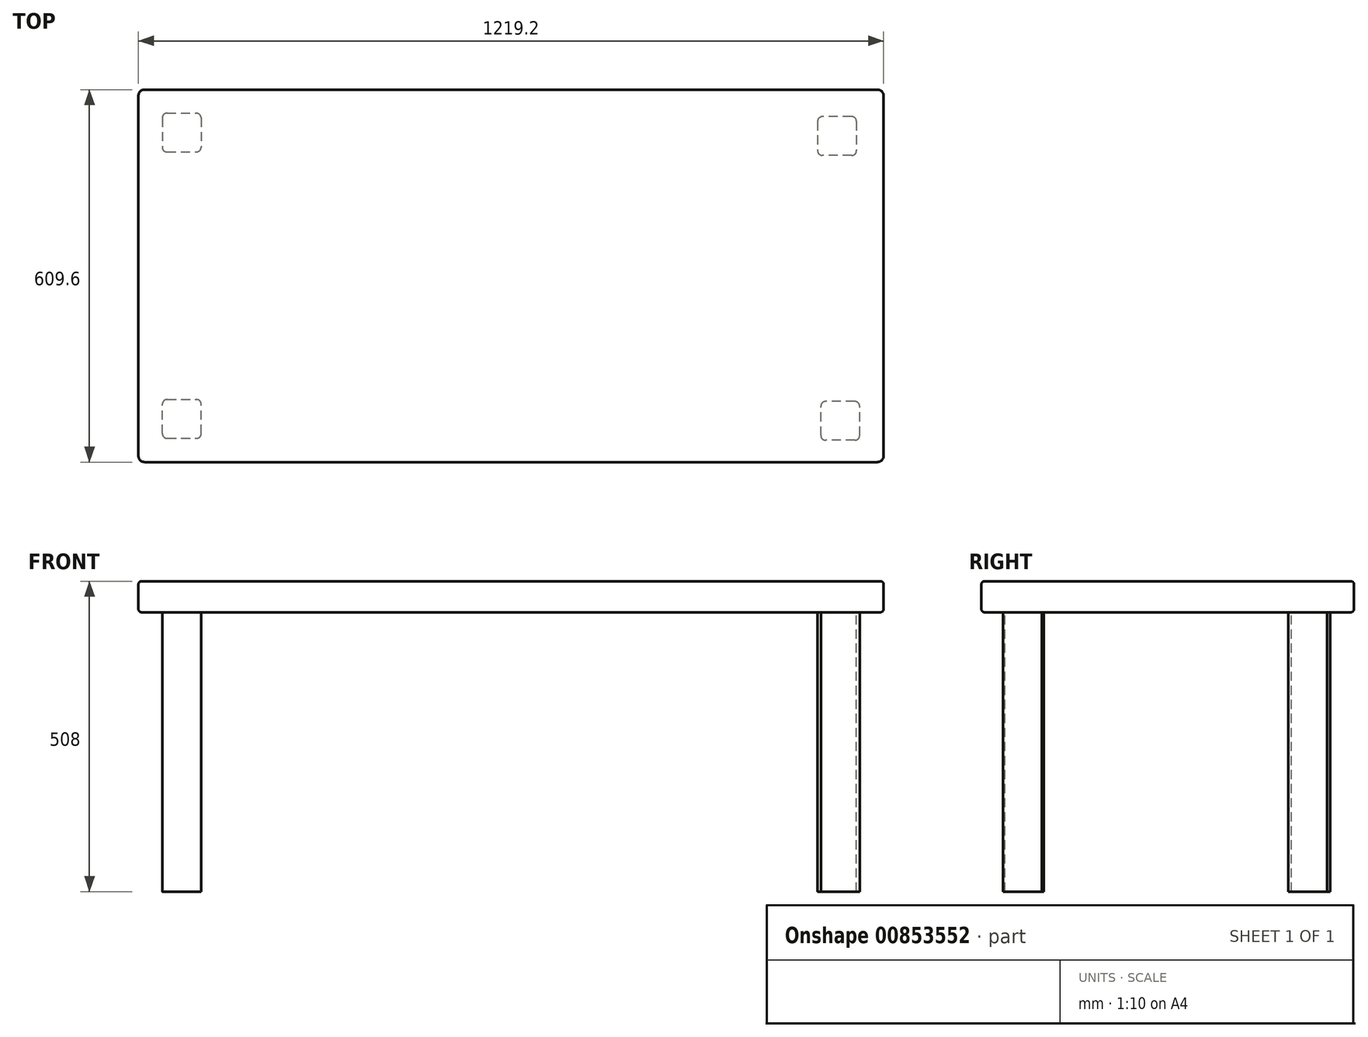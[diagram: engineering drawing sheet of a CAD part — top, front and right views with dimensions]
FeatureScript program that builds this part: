
annotation { "Feature Type Name" : "Feature", "Feature Type Description" : "" }
export const myFeature = defineFeature(function(context is Context, id is Id, definition is map)
    precondition{}
    {
        {
            var Q0;
            Q0=qCreatedBy(makeId("Front.planeOp"),FACE);
            var sketch = newSketch(context, id + "F0", { "sketchPlane" : qUnion([Q0])});
            skLineSegment(sketch, "E0.bottom", {"start": v(609.6, -25.4) * mm, "end": v(-609.6, -25.4) * mm});
            skLineSegment(sketch, "E0.top", {"start": v(609.6, 25.4) * mm, "end": v(-609.6, 25.4) * mm});
            skLineSegment(sketch, "E0.left", {"start": v(609.6, -25.4) * mm, "end": v(609.6, 25.4) * mm});
            skLineSegment(sketch, "E0.right", {"start": v(-609.6, -25.4) * mm, "end": v(-609.6, 25.4) * mm});
            skPoint(sketch, "E0.middle", {"position": v(0, 0) * mm});
            skSolve(sketch);
        }
        {
            var Q0;
            Q0 = qSketchRegion(id + "F0", true);
            extrude(context, id + "F1", {"entities" : qUnion([Q0]), "depth" : 609.6 * mm, "offsetDistance" : 25.4 * mm});
        }
        {
            var Q0;
            Q0=makeQuery(id+"F1.opExtrude","SWEPT_FACE",FACE,{"disambiguationData":[OSD([sQuery(id+"F0.wireOp",EDGE,"E0.bottom")])]});
            var sketch = newSketch(context, id + "F2", { "sketchPlane" : qUnion([Q0])});
            skLineSegment(sketch, "E1.bottom", {"start": v(-571.5, 571.5) * mm, "end": v(571.5, 571.5) * mm, "construction": true});
            skLineSegment(sketch, "E1.top", {"start": v(-571.5, 38.1) * mm, "end": v(571.5, 38.1) * mm, "construction": true});
            skLineSegment(sketch, "E1.left", {"start": v(-571.5, 571.5) * mm, "end": v(-571.5, 38.1) * mm, "construction": true});
            skLineSegment(sketch, "E1.right", {"start": v(571.5, 571.5) * mm, "end": v(571.5, 38.1) * mm, "construction": true});
            skLineSegment(sketch, "E2", {"start": v(-571.5, 571.5) * mm, "end": v(-609.6, 609.6) * mm, "construction": true});
            skLineSegment(sketch, "E3", {"start": v(571.5, 571.5) * mm, "end": v(609.6, 609.6) * mm, "construction": true});
            skLineSegment(sketch, "E4", {"start": v(-609.6, 0) * mm, "end": v(-571.5, 38.1) * mm, "construction": true});
            skLineSegment(sketch, "E5", {"start": v(571.5, 38.1) * mm, "end": v(609.6, 0) * mm, "construction": true});
            skLineSegment(sketch, "E6", {"start": v(0, 571.5) * mm, "end": v(0, 609.6) * mm, "construction": true});
            skLineSegment(sketch, "E7", {"start": v(571.5, 304.8) * mm, "end": v(609.6, 304.8) * mm, "construction": true});
            skLineSegment(sketch, "E8", {"start": v(0, 38.1) * mm, "end": v(0, 0) * mm, "construction": true});
            skLineSegment(sketch, "E9", {"start": v(-571.5, 304.8) * mm, "end": v(-609.6, 304.8) * mm, "construction": true});
            skSolve(sketch);
        }
        {
            var Q0;
            Q0=makeQuery(id+"F1.opExtrude","CAP_EDGE",EDGE,{"disambiguationData":[OSD([sQuery(id+"F0.wireOp",EDGE,"E0.right")])],"isStart":false});
            fillet(context, id + "F3", {"entities" : qUnion([Q0]), "radius" : 10.16 * mm, "tangentPropagation" : true, "allowEdgeOverflow" : false});
        }
        {
            var Q0;
            Q0=makeQuery(id+"F1.opExtrude","CAP_EDGE",EDGE,{"disambiguationData":[OSD([sQuery(id+"F0.wireOp",EDGE,"E0.right")])],"isStart":true});
            fillet(context, id + "F4", {"entities" : qUnion([Q0]), "radius" : 10.16 * mm, "tangentPropagation" : true, "allowEdgeOverflow" : false});
        }
        {
            var Q0;
            Q0=makeQuery(id+"F1.opExtrude","CAP_EDGE",EDGE,{"disambiguationData":[OSD([sQuery(id+"F0.wireOp",EDGE,"E0.left")])],"isStart":true});
            fillet(context, id + "F5", {"entities" : qUnion([Q0]), "radius" : 10.16 * mm, "tangentPropagation" : true, "allowEdgeOverflow" : false});
        }
        {
            var Q0;
            Q0=makeQuery(id+"F1.opExtrude","CAP_EDGE",EDGE,{"disambiguationData":[OSD([sQuery(id+"F0.wireOp",EDGE,"E0.left")])],"isStart":false});
            fillet(context, id + "F6", {"entities" : qUnion([Q0]), "radius" : 10.16 * mm, "tangentPropagation" : true, "allowEdgeOverflow" : false});
        }
        {
            var Q0;
            Q0=makeQuery(id+"F1.opExtrude","SWEPT_EDGE",EDGE,{"disambiguationData":[OSD([sQuery(id+"F0.wireOp",EDGE,"E0.top"),sQuery(id+"F0.wireOp",EDGE,"E0.right")])]});
            var Q1;
            Q1=makeQuery(id+"F1.opExtrude","SWEPT_EDGE",EDGE,{"disambiguationData":[OSD([sQuery(id+"F0.wireOp",EDGE,"E0.bottom"),sQuery(id+"F0.wireOp",EDGE,"E0.right")])]});
            fillet(context, id + "F7", {"entities" : qUnion([Q0, Q1]), "radius" : 5.08 * mm, "tangentPropagation" : true, "allowEdgeOverflow" : false});
        }
        {
            var Q0;
            {var subQ0=sQuery(id+"F0.wireOp",EDGE,"E0.bottom");Q0=makeQuery(id+"F2.imprint","IMPRINT",FACE,{"disambiguationData":[TD([[makeQuery(id+"F2.imprint","IMPRINT",EDGE,{"derivedFrom":makeQuery(id+"F1.opExtrude","CAP_EDGE",EDGE,{"disambiguationData":[OSD([subQ0])],"isStart":true})}),-1.0]])]});}
            var sketch = newSketch(context, id + "F8", { "sketchPlane" : qUnion([Q0])});
            skLineSegment(sketch, "E10.bottom", {"start": v(-570.63, 38.64) * mm, "end": v(-507.13, 38.64) * mm});
            skLineSegment(sketch, "E10.top", {"start": v(-570.63, 102.14) * mm, "end": v(-507.13, 102.14) * mm});
            skLineSegment(sketch, "E10.left", {"start": v(-570.63, 38.64) * mm, "end": v(-570.63, 102.14) * mm});
            skLineSegment(sketch, "E10.right", {"start": v(-507.13, 38.64) * mm, "end": v(-507.13, 102.14) * mm});
            skSolve(sketch);
        }
        {
            var Q0;
            Q0 = qSketchRegion(id + "F8", true);
            extrude(context, id + "F9", {"entities" : qUnion([Q0]), "operationType" : NewBodyOperationType.ADD, "depth" : 457.2 * mm, "offsetDistance" : 25.4 * mm});
        }
        {
            var Q0;
            Q0=makeQuery(id+"F9.opExtrude","SWEPT_EDGE",EDGE,{"disambiguationData":[OSD([sQuery(id+"F8.wireOp",EDGE,"E10.bottom"),sQuery(id+"F8.wireOp",EDGE,"E10.right")])]});
            var Q1;
            Q1=makeQuery(id+"F9.opExtrude","SWEPT_EDGE",EDGE,{"disambiguationData":[OSD([sQuery(id+"F8.wireOp",EDGE,"E10.top"),sQuery(id+"F8.wireOp",EDGE,"E10.right")])]});
            var Q2;
            Q2=makeQuery(id+"F9.opExtrude","SWEPT_EDGE",EDGE,{"disambiguationData":[OSD([sQuery(id+"F8.wireOp",EDGE,"E10.top"),sQuery(id+"F8.wireOp",EDGE,"E10.left")])]});
            var Q3;
            Q3=makeQuery(id+"F9.opExtrude","SWEPT_EDGE",EDGE,{"disambiguationData":[OSD([sQuery(id+"F8.wireOp",EDGE,"E10.bottom"),sQuery(id+"F8.wireOp",EDGE,"E10.left")])]});
            fillet(context, id + "F10", {"entities" : qUnion([Q0, Q1, Q2, Q3]), "radius" : 7.62 * mm, "tangentPropagation" : true, "allowEdgeOverflow" : false});
        }
        {
            var Q0;
            {var subQ0=sQuery(id+"F0.wireOp",EDGE,"E0.bottom");Q0=makeQuery(id+"F2.imprint","IMPRINT",FACE,{"disambiguationData":[TD([[makeQuery(id+"F2.imprint","IMPRINT",EDGE,{"derivedFrom":makeQuery(id+"F1.opExtrude","CAP_EDGE",EDGE,{"disambiguationData":[OSD([subQ0])],"isStart":true})}),-1.0]])]});}
            var sketch = newSketch(context, id + "F11", { "sketchPlane" : qUnion([Q0])});
            skLineSegment(sketch, "E11.bottom", {"start": v(565.21, 44.22) * mm, "end": v(501.71, 44.22) * mm});
            skLineSegment(sketch, "E11.top", {"start": v(565.21, 107.72) * mm, "end": v(501.71, 107.72) * mm});
            skLineSegment(sketch, "E11.left", {"start": v(565.21, 44.22) * mm, "end": v(565.21, 107.72) * mm});
            skLineSegment(sketch, "E11.right", {"start": v(501.71, 44.22) * mm, "end": v(501.71, 107.72) * mm});
            skSolve(sketch);
        }
        {
            var Q0;
            Q0 = qSketchRegion(id + "F11", true);
            extrude(context, id + "F12", {"entities" : qUnion([Q0]), "operationType" : NewBodyOperationType.ADD, "depth" : 457.2 * mm, "offsetDistance" : 25.4 * mm});
        }
        {
            var Q0;
            Q0=makeQuery(id+"F12.opExtrude","SWEPT_EDGE",EDGE,{"disambiguationData":[OSD([sQuery(id+"F11.wireOp",EDGE,"E11.top"),sQuery(id+"F11.wireOp",EDGE,"E11.left")])]});
            var Q1;
            Q1=makeQuery(id+"F12.opExtrude","SWEPT_EDGE",EDGE,{"disambiguationData":[OSD([sQuery(id+"F11.wireOp",EDGE,"E11.bottom"),sQuery(id+"F11.wireOp",EDGE,"E11.left")])]});
            var Q2;
            Q2=makeQuery(id+"F12.opExtrude","SWEPT_EDGE",EDGE,{"disambiguationData":[OSD([sQuery(id+"F11.wireOp",EDGE,"E11.top"),sQuery(id+"F11.wireOp",EDGE,"E11.right")])]});
            var Q3;
            Q3=makeQuery(id+"F12.opExtrude","SWEPT_EDGE",EDGE,{"disambiguationData":[OSD([sQuery(id+"F11.wireOp",EDGE,"E11.bottom"),sQuery(id+"F11.wireOp",EDGE,"E11.right")])]});
            fillet(context, id + "F13", {"entities" : qUnion([Q0, Q1, Q2, Q3]), "radius" : 7.62 * mm, "tangentPropagation" : true, "allowEdgeOverflow" : false});
        }
        {
            var Q0;
            {var subQ0=sQuery(id+"F0.wireOp",EDGE,"E0.bottom");Q0=makeQuery(id+"F2.imprint","IMPRINT",FACE,{"disambiguationData":[TD([[makeQuery(id+"F2.imprint","IMPRINT",EDGE,{"derivedFrom":makeQuery(id+"F1.opExtrude","CAP_EDGE",EDGE,{"disambiguationData":[OSD([subQ0])],"isStart":true})}),-1.0]])]});}
            var sketch = newSketch(context, id + "F14", { "sketchPlane" : qUnion([Q0])});
            skLineSegment(sketch, "E12.bottom", {"start": v(-570.37, 570.76) * mm, "end": v(-506.87, 570.76) * mm});
            skLineSegment(sketch, "E12.top", {"start": v(-570.37, 507.26) * mm, "end": v(-506.87, 507.26) * mm});
            skLineSegment(sketch, "E12.left", {"start": v(-570.37, 570.76) * mm, "end": v(-570.37, 507.26) * mm});
            skLineSegment(sketch, "E12.right", {"start": v(-506.87, 570.76) * mm, "end": v(-506.87, 507.26) * mm});
            skSolve(sketch);
        }
        {
            var Q0;
            Q0 = qSketchRegion(id + "F14", true);
            extrude(context, id + "F15", {"entities" : qUnion([Q0]), "operationType" : NewBodyOperationType.ADD, "depth" : 457.2 * mm, "offsetDistance" : 25.4 * mm});
        }
        {
            var Q0;
            Q0=makeQuery(id+"F15.opExtrude","SWEPT_EDGE",EDGE,{"disambiguationData":[OSD([sQuery(id+"F14.wireOp",EDGE,"E12.bottom"),sQuery(id+"F14.wireOp",EDGE,"E12.left")])]});
            var Q1;
            Q1=makeQuery(id+"F15.opExtrude","SWEPT_EDGE",EDGE,{"disambiguationData":[OSD([sQuery(id+"F14.wireOp",EDGE,"E12.bottom"),sQuery(id+"F14.wireOp",EDGE,"E12.right")])]});
            var Q2;
            Q2=makeQuery(id+"F15.opExtrude","SWEPT_EDGE",EDGE,{"disambiguationData":[OSD([sQuery(id+"F14.wireOp",EDGE,"E12.top"),sQuery(id+"F14.wireOp",EDGE,"E12.right")])]});
            var Q3;
            Q3=makeQuery(id+"F15.opExtrude","SWEPT_EDGE",EDGE,{"disambiguationData":[OSD([sQuery(id+"F14.wireOp",EDGE,"E12.top"),sQuery(id+"F14.wireOp",EDGE,"E12.left")])]});
            fillet(context, id + "F16", {"entities" : qUnion([Q0, Q1, Q2, Q3]), "radius" : 7.62 * mm, "tangentPropagation" : true, "allowEdgeOverflow" : false});
        }
        {
            var Q0;
            {var subQ0=sQuery(id+"F0.wireOp",EDGE,"E0.bottom");Q0=makeQuery(id+"F2.imprint","IMPRINT",FACE,{"disambiguationData":[TD([[makeQuery(id+"F2.imprint","IMPRINT",EDGE,{"derivedFrom":makeQuery(id+"F1.opExtrude","CAP_EDGE",EDGE,{"disambiguationData":[OSD([subQ0])],"isStart":true})}),-1.0]])]});}
            var sketch = newSketch(context, id + "F17", { "sketchPlane" : qUnion([Q0])});
            skLineSegment(sketch, "E13.bottom", {"start": v(570.38, 573.9) * mm, "end": v(506.88, 573.9) * mm});
            skLineSegment(sketch, "E13.top", {"start": v(570.38, 510.4) * mm, "end": v(506.88, 510.4) * mm});
            skLineSegment(sketch, "E13.left", {"start": v(570.38, 573.9) * mm, "end": v(570.38, 510.4) * mm});
            skLineSegment(sketch, "E13.right", {"start": v(506.88, 573.9) * mm, "end": v(506.88, 510.4) * mm});
            skSolve(sketch);
        }
        {
            var Q0;
            Q0=makeQuery(id+"F17.imprint","IMPRINT",FACE,{"disambiguationData":[TD([[makeQuery(id+"F17.imprint","IMPRINT",EDGE,{"derivedFrom":sQuery(id+"F17.wireOp",EDGE,"E13.bottom")}),1.0]])]});
            extrude(context, id + "F18", {"entities" : qUnion([Q0]), "operationType" : NewBodyOperationType.ADD, "depth" : 457.2 * mm, "offsetDistance" : 25.4 * mm});
        }
        {
            var Q0;
            Q0=makeQuery(id+"F18.opExtrude","SWEPT_EDGE",EDGE,{"disambiguationData":[OSD([sQuery(id+"F17.wireOp",EDGE,"E13.bottom"),sQuery(id+"F17.wireOp",EDGE,"E13.left")])]});
            var Q1;
            Q1=makeQuery(id+"F18.opExtrude","SWEPT_EDGE",EDGE,{"disambiguationData":[OSD([sQuery(id+"F17.wireOp",EDGE,"E13.bottom"),sQuery(id+"F17.wireOp",EDGE,"E13.right")])]});
            var Q2;
            Q2=makeQuery(id+"F18.opExtrude","SWEPT_EDGE",EDGE,{"disambiguationData":[OSD([sQuery(id+"F17.wireOp",EDGE,"E13.top"),sQuery(id+"F17.wireOp",EDGE,"E13.right")])]});
            var Q3;
            Q3=makeQuery(id+"F18.opExtrude","SWEPT_EDGE",EDGE,{"disambiguationData":[OSD([sQuery(id+"F17.wireOp",EDGE,"E13.top"),sQuery(id+"F17.wireOp",EDGE,"E13.left")])]});
            fillet(context, id + "F19", {"entities" : qUnion([Q0, Q1, Q2, Q3]), "radius" : 7.62 * mm, "tangentPropagation" : true, "allowEdgeOverflow" : false});
        }
    });
